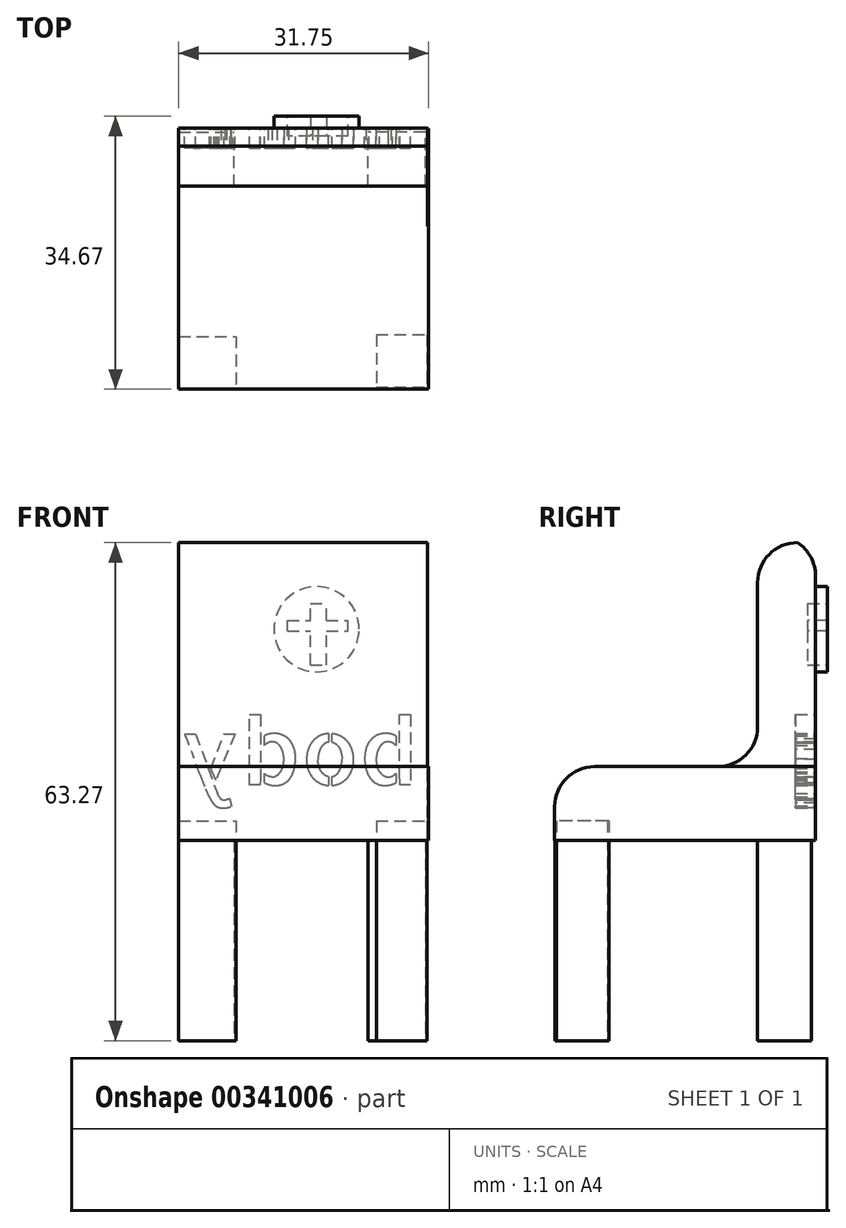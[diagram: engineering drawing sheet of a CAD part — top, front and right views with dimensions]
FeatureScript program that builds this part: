
annotation { "Feature Type Name" : "Feature", "Feature Type Description" : "" }
export const myFeature = defineFeature(function(context is Context, id is Id, definition is map)
    precondition{}
    {
        {
            var Q0;
            Q0=qCreatedBy(makeId("Top.planeOp"),FACE);
            var sketch = newSketch(context, id + "F0", { "sketchPlane" : qUnion([Q0])});
            skLineSegment(sketch, "E0.bottom", {"start": v(0, -19.09) * mm, "end": v(7.26, -19.09) * mm});
            skLineSegment(sketch, "E0.top", {"start": v(0, -25.72) * mm, "end": v(7.26, -25.72) * mm});
            skLineSegment(sketch, "E0.left", {"start": v(0, -19.09) * mm, "end": v(0, -25.72) * mm});
            skLineSegment(sketch, "E0.right", {"start": v(7.26, -19.09) * mm, "end": v(7.26, -25.72) * mm});
            skSolve(sketch);
        }
        {
            var Q0;
            Q0 = qSketchRegion(id + "F0", true);
            extrude(context, id + "F1", {"entities" : qUnion([Q0]), "depth" : 27.94 * mm});
        }
        {
            var Q0;
            Q0=qCreatedBy(makeId("Top.planeOp"),FACE);
            var sketch = newSketch(context, id + "F2", { "sketchPlane" : qUnion([Q0])});
            skLineSegment(sketch, "E1.bottom", {"start": v(0, 0) * mm, "end": v(7.05, 0) * mm});
            skLineSegment(sketch, "E1.top", {"start": v(0, 6.85) * mm, "end": v(7.05, 6.85) * mm});
            skLineSegment(sketch, "E1.left", {"start": v(0, 0) * mm, "end": v(0, 6.85) * mm});
            skLineSegment(sketch, "E1.right", {"start": v(7.05, 0) * mm, "end": v(7.05, 6.85) * mm});
            skSolve(sketch);
        }
        {
            var Q0;
            Q0 = qSketchRegion(id + "F2", true);
            extrude(context, id + "F3", {"entities" : qUnion([Q0]), "depth" : 27.94 * mm});
        }
        {
            var Q0;
            Q0=qCreatedBy(makeId("Top.planeOp"),FACE);
            var sketch = newSketch(context, id + "F4", { "sketchPlane" : qUnion([Q0])});
            skLineSegment(sketch, "E2.bottom", {"start": v(31.33, 0) * mm, "end": v(24.07, 0) * mm});
            skLineSegment(sketch, "E2.top", {"start": v(31.33, 6.85) * mm, "end": v(24.07, 6.85) * mm});
            skLineSegment(sketch, "E2.left", {"start": v(31.33, 0) * mm, "end": v(31.33, 6.85) * mm});
            skLineSegment(sketch, "E2.right", {"start": v(24.07, 0) * mm, "end": v(24.07, 6.85) * mm});
            skSolve(sketch);
        }
        {
            var Q0;
            Q0 = qSketchRegion(id + "F4", true);
            extrude(context, id + "F5", {"entities" : qUnion([Q0]), "depth" : 27.94 * mm});
        }
        {
            var Q0;
            Q0=qCreatedBy(makeId("Top.planeOp"),FACE);
            var sketch = newSketch(context, id + "F6", { "sketchPlane" : qUnion([Q0])});
            skLineSegment(sketch, "E3.bottom", {"start": v(25.1, -18.88) * mm, "end": v(31.53, -18.88) * mm});
            skLineSegment(sketch, "E3.top", {"start": v(25.1, -25.52) * mm, "end": v(31.53, -25.52) * mm});
            skLineSegment(sketch, "E3.left", {"start": v(25.1, -18.88) * mm, "end": v(25.1, -25.52) * mm});
            skLineSegment(sketch, "E3.right", {"start": v(31.53, -18.88) * mm, "end": v(31.53, -25.52) * mm});
            skSolve(sketch);
        }
        {
            var Q0;
            Q0 = qSketchRegion(id + "F6", true);
            extrude(context, id + "F7", {"entities" : qUnion([Q0]), "depth" : 27.94 * mm});
        }
        {
            var Q0;
            Q0=qCreatedBy(makeId("Right.planeOp"),FACE);
            var sketch = newSketch(context, id + "F8", { "sketchPlane" : qUnion([Q0])});
            skLineSegment(sketch, "E4.bottom", {"start": v(-25.78, 34.81) * mm, "end": v(7.33, 34.81) * mm});
            skLineSegment(sketch, "E4.top", {"start": v(-25.78, 25.44) * mm, "end": v(7.33, 25.44) * mm});
            skLineSegment(sketch, "E4.left", {"start": v(-25.78, 34.81) * mm, "end": v(-25.78, 25.44) * mm});
            skLineSegment(sketch, "E4.right", {"start": v(7.33, 34.81) * mm, "end": v(7.33, 25.44) * mm});
            skSolve(sketch);
        }
        {
            var Q0;
            Q0 = qSketchRegion(id + "F8", true);
            extrude(context, id + "F9", {"entities" : qUnion([Q0]), "depth" : 31.75 * mm});
        }
        {
            var Q0;
            Q0=qCreatedBy(makeId("Front.planeOp"),FACE);
            var sketch = newSketch(context, id + "F10", { "sketchPlane" : qUnion([Q0])});
            skLineSegment(sketch, "E5.bottom", {"start": v(0, 25.46) * mm, "end": v(31.61, 25.46) * mm});
            skLineSegment(sketch, "E5.top", {"start": v(0, 63.27) * mm, "end": v(31.61, 63.27) * mm});
            skLineSegment(sketch, "E5.left", {"start": v(0, 25.46) * mm, "end": v(0, 63.27) * mm});
            skLineSegment(sketch, "E5.right", {"start": v(31.61, 25.46) * mm, "end": v(31.61, 63.27) * mm});
            skSolve(sketch);
        }
        {
            var Q0;
            Q0 = qSketchRegion(id + "F10", true);
            extrude(context, id + "F11", {"entities" : qUnion([Q0]), "operationType" : NewBodyOperationType.ADD, "oppositeDirection" : true, "depth" : 7.37 * mm});
        }
        {
            var Q0;
            Q0=makeQuery(id+"F11.opExtrude","CAP_EDGE",EDGE,{"disambiguationData":[OSD([sQuery(id+"F10.wireOp",EDGE,"E5.top")])],"isStart":true});
            fillet(context, id + "F12", {"entities" : qUnion([Q0]), "radius" : 5.08 * mm, "tangentPropagation" : true, "allowEdgeOverflow" : false});
        }
        {
            var Q0;
            Q0=makeQuery(id+"F11.opExtrude","CAP_EDGE",EDGE,{"disambiguationData":[OSD([sQuery(id+"F10.wireOp",EDGE,"E5.top")])],"isStart":false});
            fillet(context, id + "F13", {"entities" : qUnion([Q0]), "radius" : 5.08 * mm, "tangentPropagation" : true, "allowEdgeOverflow" : false});
        }
        {
            var Q0;
            Q0=makeQuery(id+"F9.opExtrude","SWEPT_EDGE",EDGE,{"disambiguationData":[OSD([sQuery(id+"F8.wireOp",EDGE,"E4.bottom"),sQuery(id+"F8.wireOp",EDGE,"E4.left")])]});
            fillet(context, id + "F14", {"entities" : qUnion([Q0]), "radius" : 5.08 * mm, "tangentPropagation" : true, "allowEdgeOverflow" : false});
        }
        {
            var Q0;
            Q0=qCreatedBy(makeId("Front.planeOp"),FACE);
            var sketch = newSketch(context, id + "F15", { "sketchPlane" : qUnion([Q0])});
            skCircle(sketch, "E6", {"center": v(17.51, 52.27) * mm, "radius": 5.4 * mm});
            skSolve(sketch);
        }
        {
            var Q0;
            Q0 = qSketchRegion(id + "F15", true);
            extrude(context, id + "F16", {"entities" : qUnion([Q0]), "operationType" : NewBodyOperationType.ADD, "oppositeDirection" : true, "depth" : 8.9 * mm});
        }
        {
            var Q0;
            Q0=makeQuery(id+"F16.opExtrude","CAP_FACE",FACE,{"disambiguationData":[OSD([sQuery(id+"F15.wireOp",EDGE,"E6")])],"isStart":false});
            cPlane(context, id + "F17", {"entities" : qUnion([Q0]), "cplaneType" : CPlaneType.OFFSET, "offset" : 25.4 * mm, "width" : 152.4 * mm, "height" : 152.4 * mm});
        }
        {
            var Q0;
            Q0=qCreatedBy(id+"F17.planeOp",FACE);
            var sketch = newSketch(context, id + "F18", { "sketchPlane" : qUnion([Q0])});
            skLineSegment(sketch, "E7.bottom", {"start": v(-21.5, 53.4) * mm, "end": v(-13.8, 53.4) * mm});
            skLineSegment(sketch, "E7.top", {"start": v(-21.5, 52.04) * mm, "end": v(-13.8, 52.04) * mm});
            skLineSegment(sketch, "E7.left", {"start": v(-21.5, 53.4) * mm, "end": v(-21.5, 52.04) * mm});
            skLineSegment(sketch, "E7.right", {"start": v(-13.8, 53.4) * mm, "end": v(-13.8, 52.04) * mm});
            skSolve(sketch);
        }
        {
            var Q0;
            Q0 = qSketchRegion(id + "F18", true);
            extrude(context, id + "F19", {"entities" : qUnion([Q0]), "operationType" : NewBodyOperationType.REMOVE, "oppositeDirection" : true, "depth" : 27.94 * mm});
        }
        {
            var Q0;
            Q0=qCreatedBy(id+"F17.planeOp",FACE);
            var sketch = newSketch(context, id + "F20", { "sketchPlane" : qUnion([Q0])});
            skLineSegment(sketch, "E8.bottom", {"start": v(-18.77, 55.52) * mm, "end": v(-16.74, 55.52) * mm});
            skLineSegment(sketch, "E8.top", {"start": v(-18.77, 47.7) * mm, "end": v(-16.74, 47.7) * mm});
            skLineSegment(sketch, "E8.left", {"start": v(-18.77, 55.52) * mm, "end": v(-18.77, 47.7) * mm});
            skLineSegment(sketch, "E8.right", {"start": v(-16.74, 55.52) * mm, "end": v(-16.74, 47.7) * mm});
            skSolve(sketch);
        }
        {
            var Q0;
            Q0 = qSketchRegion(id + "F20", true);
            extrude(context, id + "F21", {"entities" : qUnion([Q0]), "operationType" : NewBodyOperationType.REMOVE, "oppositeDirection" : true, "depth" : 27.94 * mm});
        }
        {
            var Q0;
            Q0=makeQuery(id+"F11.boolean.opBoolean","INTERSECT",EDGE,{"derivedFrom":[makeQuery(id+"F9.opExtrude","SWEPT_FACE",FACE,{"disambiguationData":[OSD([sQuery(id+"F8.wireOp",EDGE,"E4.bottom")])]}),makeQuery(id+"F11.opExtrude","CAP_FACE",FACE,{"disambiguationData":[OSD([sQuery(id+"F10.wireOp",EDGE,"E5.bottom"),sQuery(id+"F10.wireOp",EDGE,"E5.top"),sQuery(id+"F10.wireOp",EDGE,"E5.left"),sQuery(id+"F10.wireOp",EDGE,"E5.right")])],"isStart":true})]});
            fillet(context, id + "F22", {"entities" : qUnion([Q0]), "radius" : 5.08 * mm, "tangentPropagation" : true, "allowEdgeOverflow" : false});
        }
        {
            var Q0;
            Q0=makeQuery(id+"F11.opExtrude","CAP_EDGE",EDGE,{"disambiguationData":[OSD([sQuery(id+"F10.wireOp",EDGE,"E5.bottom")])],"isStart":false});
            fillet(context, id + "F23", {"entities" : qUnion([Q0]), "radius" : 5.08 * mm, "tangentPropagation" : true, "allowEdgeOverflow" : false});
        }
        {
            var Q0;
            Q0=makeQuery(id+"F11.opExtrude","CAP_FACE",FACE,{"disambiguationData":[OSD([sQuery(id+"F10.wireOp",EDGE,"E5.bottom"),sQuery(id+"F10.wireOp",EDGE,"E5.top"),sQuery(id+"F10.wireOp",EDGE,"E5.left"),sQuery(id+"F10.wireOp",EDGE,"E5.right")])],"isStart":false});
            cPlane(context, id + "F24", {"entities" : qUnion([Q0]), "cplaneType" : CPlaneType.OFFSET, "offset" : 25.4 * mm, "width" : 152.4 * mm, "height" : 152.4 * mm});
        }
        {
            var Q0;
            Q0=qCreatedBy(id+"F24.planeOp",FACE);
            var sketch = newSketch(context, id + "F25", { "sketchPlane" : qUnion([Q0])});
            skText(sketch, "E9", { "text": "body", "fontName": "AllertaStencil-Regular.ttf"});
            const initialGuessF25  = {"E9": [-0.03044, 0.03247, 1, 0, 0.0085]};
            skSetInitialGuess(sketch, initialGuessF25);
            skSolve(sketch);
        }
        {
            var Q0;
            Q0 = qSketchRegion(id + "F25", true);
            extrude(context, id + "F26", {"entities" : qUnion([Q0]), "operationType" : NewBodyOperationType.REMOVE, "oppositeDirection" : true, "depth" : 27.94 * mm});
        }
    });
